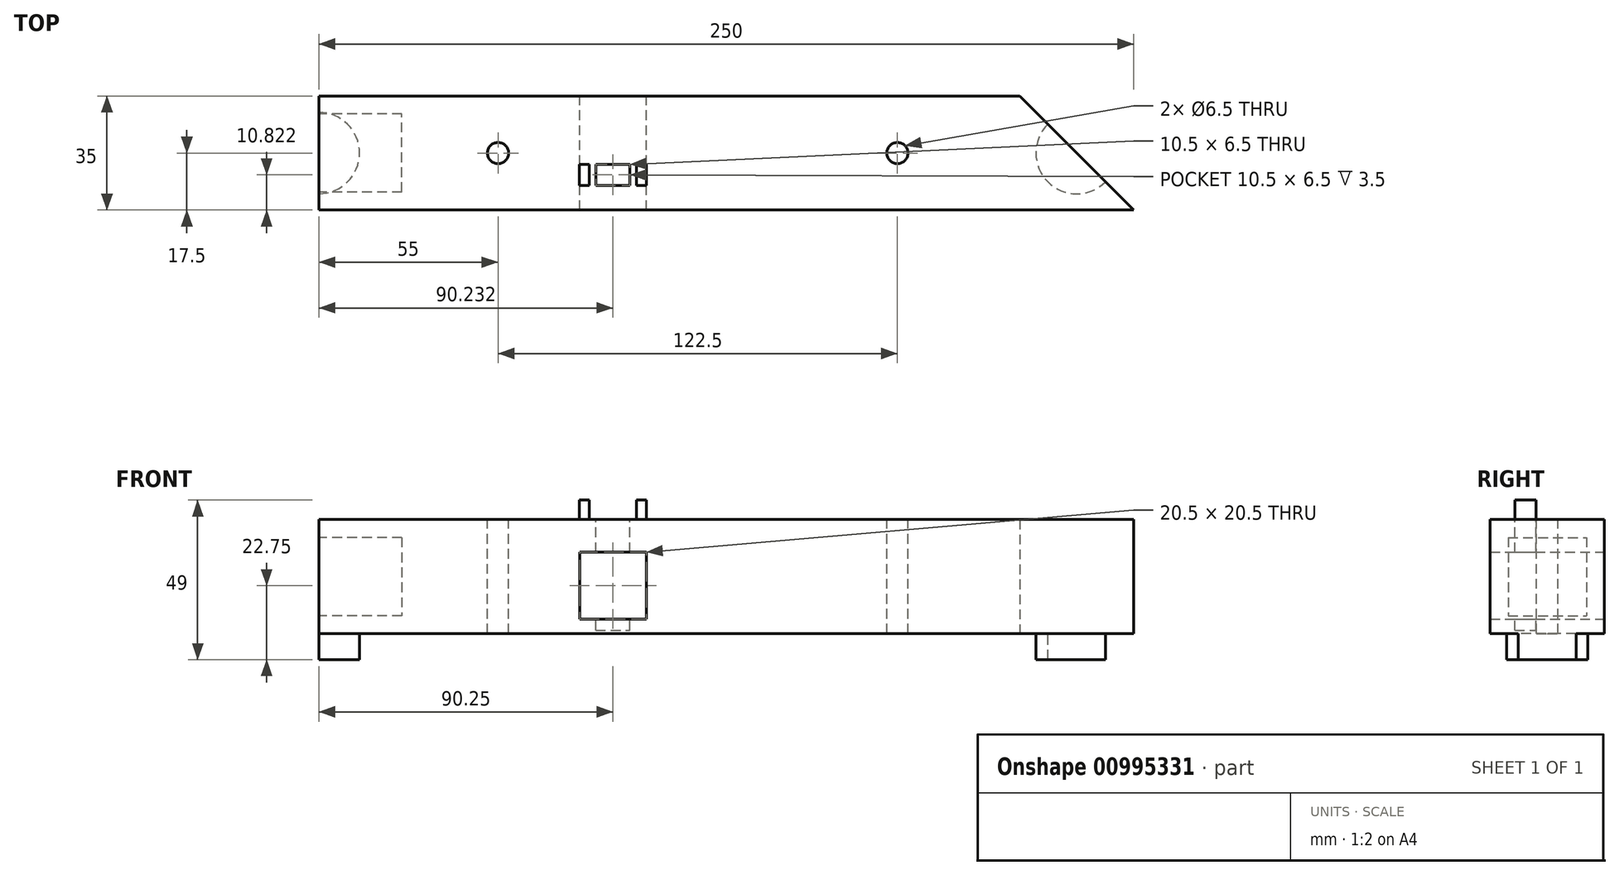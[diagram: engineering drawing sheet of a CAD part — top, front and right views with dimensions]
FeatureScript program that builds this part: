
annotation { "Feature Type Name" : "Feature", "Feature Type Description" : "" }
export const myFeature = defineFeature(function(context is Context, id is Id, definition is map)
    precondition{}
    {
        {
            var Q0;
            Q0=qCreatedBy(makeId("Top.planeOp"),FACE);
            var sketch = newSketch(context, id + "F0", { "sketchPlane" : qUnion([Q0])});
            skLineSegment(sketch, "E0.bottom", {"start": v(125, -17.5) * mm, "end": v(-125, -17.5) * mm});
            skLineSegment(sketch, "E0.top", {"start": v(90, 17.5) * mm, "end": v(-125, 17.5) * mm});
            skLineSegment(sketch, "E0.right", {"start": v(-125, -17.5) * mm, "end": v(-125, 17.5) * mm});
            skPoint(sketch, "E0.middle", {"position": v(0, 0) * mm});
            skPoint(sketch, "E1", {"position": v(90, 17.5) * mm});
            skLineSegment(sketch, "E2", {"start": v(125, -17.5) * mm, "end": v(90, 17.5) * mm});
            skPoint(sketch, "E0.left.end.orphan", {"position": v(125, 17.5) * mm});
            skSolve(sketch);
        }
        {
            var Q0;
            Q0=makeQuery(id+"F0.imprint","IMPRINT",FACE,{"disambiguationData":[TD([[makeQuery(id+"F0.imprint","IMPRINT",EDGE,{"derivedFrom":sQuery(id+"F0.wireOp",EDGE,"E0.bottom")}),-1.0]])]});
            extrude(context, id + "F1", {"entities" : qUnion([Q0]), "depth" : 35 * mm, "offsetDistance" : 25 * mm});
        }
        {
            var Q0;
            Q0=makeQuery(id+"F1.opExtrude","SWEPT_FACE",FACE,{"disambiguationData":[OSD([sQuery(id+"F0.wireOp",EDGE,"E0.right")])]});
            var sketch = newSketch(context, id + "F2", { "sketchPlane" : qUnion([Q0])});
            skLineSegment(sketch, "E3.0", {"start": v(-12, 29.5) * mm, "end": v(-12, 5.5) * mm});
            skLineSegment(sketch, "E3.1", {"start": v(12, 29.5) * mm, "end": v(-12, 29.5) * mm});
            skLineSegment(sketch, "E4.0", {"start": v(12, 5.5) * mm, "end": v(-12, 5.5) * mm});
            skLineSegment(sketch, "E4.1", {"start": v(12, 29.5) * mm, "end": v(12, 5.5) * mm});
            skSolve(sketch);
        }
        {
            var Q0;
            Q0=makeQuery(id+"F2.imprint","IMPRINT",FACE,{"disambiguationData":[TD([[makeQuery(id+"F2.imprint","IMPRINT",EDGE,{"derivedFrom":sQuery(id+"F2.wireOp",EDGE,"E3.0")}),1.0]])]});
            extrude(context, id + "F3", {"entities" : qUnion([Q0]), "operationType" : NewBodyOperationType.REMOVE, "oppositeDirection" : true, "depth" : 25.5 * mm, "offsetDistance" : 25 * mm});
        }
        {
            var Q0;
            Q0=makeQuery(id+"F1.opExtrude","CAP_FACE",FACE,{"disambiguationData":[OSD([sQuery(id+"F0.wireOp",EDGE,"E0.bottom"),sQuery(id+"F0.wireOp",EDGE,"E0.top"),sQuery(id+"F0.wireOp",EDGE,"E0.right"),sQuery(id+"F0.wireOp",EDGE,"E2")])],"isStart":false});
            var sketch = newSketch(context, id + "F4", { "sketchPlane" : qUnion([Q0])});
            skPoint(sketch, "E5", {"position": v(52.5, 0) * mm});
            skPoint(sketch, "E6", {"position": v(107.5, 0) * mm});
            skPoint(sketch, "E7", {"position": v(-125, 0) * mm});
            skPoint(sketch, "E8", {"position": v(-70, 0) * mm});
            skSolve(sketch);
        }
        {
            var Q0;
            Q0=sQuery(id+"F4.wireOp",VERTEX,"E5");
            var Q1;
            Q1=sQuery(id+"F4.wireOp",VERTEX,"E8");
            var Q2;
            Q2=makeQuery(id+"F1.opExtrude","SWEPT_BODY",BODY,{"disambiguationData":[OSD([sQuery(id+"F0.wireOp",EDGE,"E0.bottom"),sQuery(id+"F0.wireOp",EDGE,"E0.top"),sQuery(id+"F0.wireOp",EDGE,"E0.right"),sQuery(id+"F0.wireOp",EDGE,"E2")])]});
            hole(context, id + "F5", {"style" : HoleStyle.SIMPLE, "endStyle" : HoleEndStyle.BLIND, "holeDiameter" : 6.5 * mm, "majorDiameter" : 5 * mm, "holeDepth" : 35 * mm, "isTappedThrough" : true, "tappedDepth" : 12 * mm, "tapClearance" : 3, "locations" : qUnion([Q0, Q1]), "scope" : qUnion([Q2])});
        }
        {
            var Q0;
            Q0=makeQuery(id+"F1.opExtrude","CAP_FACE",FACE,{"disambiguationData":[OSD([sQuery(id+"F0.wireOp",EDGE,"E0.bottom"),sQuery(id+"F0.wireOp",EDGE,"E0.top"),sQuery(id+"F0.wireOp",EDGE,"E0.right"),sQuery(id+"F0.wireOp",EDGE,"E2")])],"isStart":true});
            var sketch = newSketch(context, id + "F6", { "sketchPlane" : qUnion([Q0])});
            skCircle(sketch, "E9", {"center": v(107.5, 0) * mm, "radius": 12.5 * mm});
            skSolve(sketch);
        }
        {
            var Q0;
            {var subQ0=sQuery(id+"F6.wireOp",EDGE,"E9");var subQ1=makeQuery(id+"F1.opExtrude","CAP_EDGE",EDGE,{"disambiguationData":[OSD([sQuery(id+"F0.wireOp",EDGE,"E2")])],"isStart":true});var subQ2=makeQuery(id+"F6.imprint","INTERSECT",VERTEX,{"disambiguationData":[OD(0.0)],"derivedFrom":[subQ1,subQ0]});Q0=makeQuery(id+"F6.imprint","IMPRINT",FACE,{"disambiguationData":[TD([[makeQuery(id+"F6.imprint","IMPRINT",EDGE,{"disambiguationData":[TD([[subQ2,-1.0]])],"derivedFrom":subQ0}),1.0]])]});}
            extrude(context, id + "F7", {"entities" : qUnion([Q0]), "operationType" : NewBodyOperationType.ADD, "depth" : 8 * mm, "offsetDistance" : 25 * mm});
        }
        {
            var Q0;
            Q0=makeQuery(id+"F1.opExtrude","CAP_FACE",FACE,{"disambiguationData":[OSD([sQuery(id+"F0.wireOp",EDGE,"E0.bottom"),sQuery(id+"F0.wireOp",EDGE,"E0.top"),sQuery(id+"F0.wireOp",EDGE,"E0.right"),sQuery(id+"F0.wireOp",EDGE,"E2")])],"isStart":true});
            var sketch = newSketch(context, id + "F8", { "sketchPlane" : qUnion([Q0])});
            skCircle(sketch, "E10", {"center": v(-125, 0) * mm, "radius": 12.5 * mm});
            skSolve(sketch);
        }
        {
            var Q0;
            {var subQ0=sQuery(id+"F8.wireOp",EDGE,"E10");var subQ1=makeQuery(id+"F1.opExtrude","CAP_EDGE",EDGE,{"disambiguationData":[OSD([sQuery(id+"F0.wireOp",EDGE,"E0.right")])],"isStart":true});var subQ2=makeQuery(id+"F8.imprint","INTERSECT",VERTEX,{"disambiguationData":[OD(0.0)],"derivedFrom":[subQ1,subQ0]});Q0=makeQuery(id+"F8.imprint","IMPRINT",FACE,{"disambiguationData":[TD([[makeQuery(id+"F8.imprint","IMPRINT",EDGE,{"disambiguationData":[TD([[subQ2,1.0]])],"derivedFrom":subQ0}),1.0]])]});}
            extrude(context, id + "F9", {"entities" : qUnion([Q0]), "operationType" : NewBodyOperationType.ADD, "depth" : 8 * mm, "offsetDistance" : 25 * mm});
        }
        {
            var Q0;
            Q0=makeQuery(id+"F1.opExtrude","SWEPT_FACE",FACE,{"disambiguationData":[OSD([sQuery(id+"F0.wireOp",EDGE,"E0.top")])]});
            var sketch = newSketch(context, id + "F10", { "sketchPlane" : qUnion([Q0])});
            skPoint(sketch, "E11", {"position": v(45, 25) * mm});
            skLineSegment(sketch, "E12.bottom", {"start": v(45, 25) * mm, "end": v(24.5, 25) * mm});
            skLineSegment(sketch, "E12.top", {"start": v(45, 4.5) * mm, "end": v(24.5, 4.5) * mm});
            skLineSegment(sketch, "E12.left", {"start": v(45, 25) * mm, "end": v(45, 4.5) * mm});
            skLineSegment(sketch, "E12.right", {"start": v(24.5, 25) * mm, "end": v(24.5, 4.5) * mm});
            skSolve(sketch);
        }
        {
            var Q0;
            Q0=qSketchRegion(id+"F10",true);
            extrude(context, id + "F11", {"entities" : qUnion([Q0]), "operationType" : NewBodyOperationType.REMOVE, "oppositeDirection" : true, "depth" : 100 * mm, "offsetDistance" : 25 * mm});
        }
        {
            var Q0;
            Q0=makeQuery(id+"F1.opExtrude","CAP_FACE",FACE,{"disambiguationData":[OSD([sQuery(id+"F0.wireOp",EDGE,"E0.bottom"),sQuery(id+"F0.wireOp",EDGE,"E0.top"),sQuery(id+"F0.wireOp",EDGE,"E0.right"),sQuery(id+"F0.wireOp",EDGE,"E2")])],"isStart":false});
            var sketch = newSketch(context, id + "F12", { "sketchPlane" : qUnion([Q0])});
            skPoint(sketch, "E13", {"position": v(-40.02, -9.93) * mm});
            skLineSegment(sketch, "E14.bottom", {"start": v(-40.02, -9.93) * mm, "end": v(-29.52, -9.93) * mm});
            skLineSegment(sketch, "E14.top", {"start": v(-40.02, -3.43) * mm, "end": v(-29.52, -3.43) * mm});
            skLineSegment(sketch, "E14.left", {"start": v(-40.02, -9.93) * mm, "end": v(-40.02, -3.43) * mm});
            skLineSegment(sketch, "E14.right", {"start": v(-29.52, -9.93) * mm, "end": v(-29.52, -3.43) * mm});
            skLineSegment(sketch, "E15", {"start": v(-60.73, 0) * mm, "end": v(-19.7, 0) * mm});
            skLineSegment(sketch, "E16.MirrorCS", {"start": v(-40.02, 3.43) * mm, "end": v(-29.52, 3.43) * mm});
            skPoint(sketch, "E17.MirrorP", {"position": v(-40.02, 9.93) * mm});
            skLineSegment(sketch, "E18.MirrorCS", {"start": v(-40.02, 9.93) * mm, "end": v(-40.02, 3.43) * mm});
            skLineSegment(sketch, "E19.MirrorCS", {"start": v(-40.02, 9.93) * mm, "end": v(-29.52, 9.93) * mm});
            skLineSegment(sketch, "E20.MirrorCS", {"start": v(-29.52, 9.93) * mm, "end": v(-29.52, 3.43) * mm});
            skPoint(sketch, "E21", {"position": v(-24.52, 9.93) * mm});
            skPoint(sketch, "E22", {"position": v(-45.02, 9.93) * mm});
            skLineSegment(sketch, "E23.bottom", {"start": v(-24.52, 9.93) * mm, "end": v(-27.52, 9.93) * mm});
            skLineSegment(sketch, "E23.top", {"start": v(-24.52, 3.43) * mm, "end": v(-27.52, 3.43) * mm});
            skLineSegment(sketch, "E23.left", {"start": v(-24.52, 9.93) * mm, "end": v(-24.52, 3.43) * mm});
            skLineSegment(sketch, "E23.right", {"start": v(-27.52, 9.93) * mm, "end": v(-27.52, 3.43) * mm});
            skLineSegment(sketch, "E24.bottom", {"start": v(-45.02, 9.93) * mm, "end": v(-42.02, 9.93) * mm});
            skLineSegment(sketch, "E24.top", {"start": v(-45.02, 3.43) * mm, "end": v(-42.02, 3.43) * mm});
            skLineSegment(sketch, "E24.left", {"start": v(-45.02, 9.93) * mm, "end": v(-45.02, 3.43) * mm});
            skLineSegment(sketch, "E24.right", {"start": v(-42.02, 9.93) * mm, "end": v(-42.02, 3.43) * mm});
            skLineSegment(sketch, "E25.MirrorCS", {"start": v(-24.52, -3.43) * mm, "end": v(-27.52, -3.43) * mm});
            skLineSegment(sketch, "E26.MirrorCS", {"start": v(-24.52, -9.93) * mm, "end": v(-24.52, -3.43) * mm});
            skLineSegment(sketch, "E27.MirrorCS", {"start": v(-27.52, -9.93) * mm, "end": v(-27.52, -3.43) * mm});
            skLineSegment(sketch, "E28.MirrorCS", {"start": v(-24.52, -9.93) * mm, "end": v(-27.52, -9.93) * mm});
            skLineSegment(sketch, "E29.MirrorCS", {"start": v(-42.02, -9.93) * mm, "end": v(-42.02, -3.43) * mm});
            skLineSegment(sketch, "E30.MirrorCS", {"start": v(-45.02, -3.43) * mm, "end": v(-42.02, -3.43) * mm});
            skLineSegment(sketch, "E31.MirrorCS", {"start": v(-45.02, -9.93) * mm, "end": v(-45.02, -3.43) * mm});
            skLineSegment(sketch, "E32.MirrorCS", {"start": v(-45.02, -9.93) * mm, "end": v(-42.02, -9.93) * mm});
            skSolve(sketch);
        }
        {
            var Q0;
            Q0=makeQuery(id+"F12.imprint","IMPRINT",FACE,{"disambiguationData":[TD([[makeQuery(id+"F12.imprint","IMPRINT",EDGE,{"derivedFrom":sQuery(id+"F12.wireOp",EDGE,"E14.bottom")}),1.0]])]});
            extrude(context, id + "F13", {"entities" : qUnion([Q0]), "operationType" : NewBodyOperationType.REMOVE, "oppositeDirection" : true, "depth" : 34 * mm, "offsetDistance" : 25 * mm});
        }
        {
            var Q0;
            Q0=makeQuery(id+"F12.imprint","IMPRINT",FACE,{"disambiguationData":[TD([[makeQuery(id+"F12.imprint","IMPRINT",EDGE,{"derivedFrom":sQuery(id+"F12.wireOp",EDGE,"E25.MirrorCS")}),1.0]])]});
            var Q1;
            Q1=makeQuery(id+"F12.imprint","IMPRINT",FACE,{"disambiguationData":[TD([[makeQuery(id+"F12.imprint","IMPRINT",EDGE,{"derivedFrom":sQuery(id+"F12.wireOp",EDGE,"E29.MirrorCS")}),1.0]])]});
            extrude(context, id + "F14", {"entities" : qUnion([Q0, Q1]), "operationType" : NewBodyOperationType.ADD, "depth" : 6 * mm, "offsetDistance" : 25 * mm});
        }
    });
